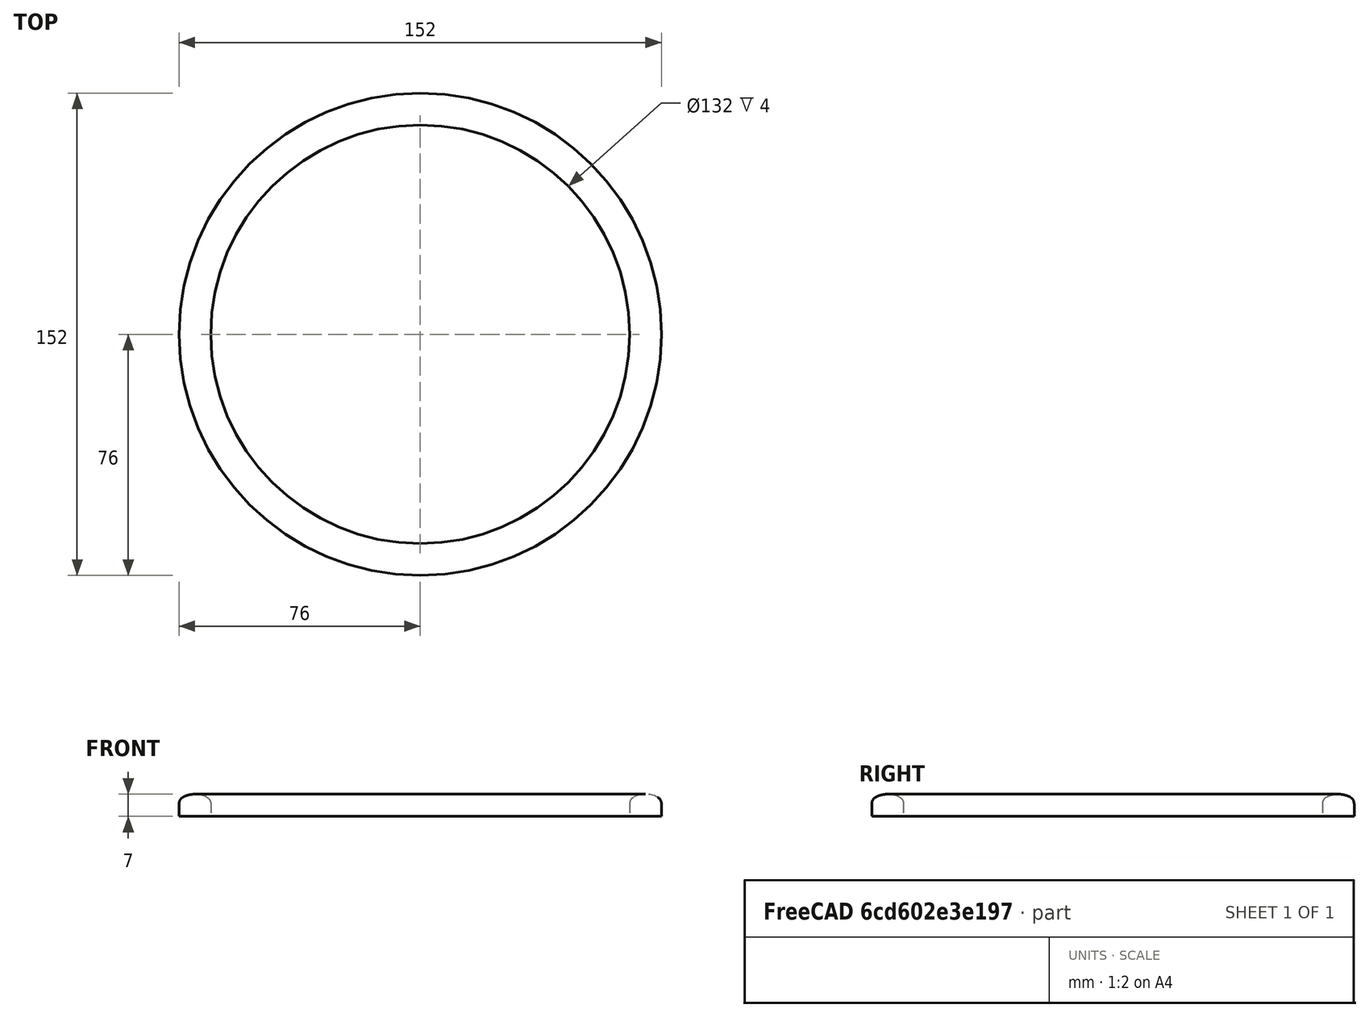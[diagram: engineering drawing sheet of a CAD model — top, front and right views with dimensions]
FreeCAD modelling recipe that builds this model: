
FCSTD DOCUMENT  (FreeCAD 0.18R14016 (Git))
Label: input_rim_test1
License: All rights reserved
LicenseURL: http://en.wikipedia.org/wiki/All_rights_reserved
objects: Sketcher::SketchObject×2, PartDesign::Revolution×1, PartDesign::Body×1, Part::Part2DObjectPython×1, TechDraw::DrawSVGTemplate×1, TechDraw::DrawViewPart×1, TechDraw::DrawPage×1
note: 6 computed .brp shape members not serialized (recipe doc carries the construction recipe); baked Part::Feature solids carry a one-line shape summary decoded from their .brp

FEATURE [Sketcher::SketchObject] Sketch  label="input_rim_base_Sketch"
  MapMode = 5
  Placement = pos=(0,0,0) rot=(1,0,0;1.5708rad)
  Support = -> [XZ_Plane]
  sketch-geometry (8):
    g0: LineSegment StartX=66 StartY=0 StartZ=0 EndX=76 EndY=0 EndZ=0
    g1: LineSegment [constr] StartX=66 StartY=0 StartZ=0 EndX=0 EndY=0 EndZ=0
    g2: LineSegment StartX=76 StartY=0 StartZ=0 EndX=76 EndY=4 EndZ=0
    g3: ArcOfCircle CenterX=73.6667 CenterY=4 CenterZ=0 NormalX=0 NormalY=0 NormalZ=1 AngleXU=0 Radius=2.33333 StartAngle=0 EndAngle=1.08084
    g4: ArcOfCircle CenterX=71 CenterY=-1 CenterZ=0 NormalX=0 NormalY=0 NormalZ=1 AngleXU=0 Radius=8 StartAngle=1.08084 EndAngle=2.06075
    g5: ArcOfCircle CenterX=68.3333 CenterY=4 CenterZ=0 NormalX=0 NormalY=0 NormalZ=1 AngleXU=0 Radius=2.33333 StartAngle=2.06075 EndAngle=3.14159
    g6: LineSegment StartX=66 StartY=4 StartZ=0 EndX=66 EndY=0 EndZ=0
    g7: LineSegment [constr] StartX=71 StartY=7 StartZ=0 EndX=71 EndY=0 EndZ=0
  constraints (22):
    c: Horizontal(g0)
    c: Coincident(g1,g0)
    c: Coincident(g1,g-1)
    c: Horizontal(g1)
    c: DistanceX(g0,g0) = 10
    c: Coincident(g0,g2)
    c: Vertical(g2)
    c: Tangent(g2,g3) = -1.5708
    c: Tangent(g3,g4) = -1.5708
    c: Tangent(g4,g5) = -1.5708
    c: Tangent(g5,g6) = -1.5708
    c: Coincident(g6,g0)
    c: Vertical(g6)
    c: Equal(g3,g5)
    c: Vertical(g7)
    c: Symmetric(g0,g0,g7)
    c: Perpendicular(g7,g4) = 4.71239
    c: DistanceY(g7,g7) = 7
    c: Radius(g5) = 2.33333
    c: DistanceX(g1,g1) = 66
    c: Radius(g4) = 8
    c: DistanceY(g2,g2) = 4
FEATURE [PartDesign::Revolution] Revolution
  Angle = 360
  Axis = (0,0,1)
  Base = (0,0,0)
  Placement = pos=(0,0,0) rot=(1,0,0;1.5708rad)
  Profile = -> Sketch
  ReferenceAxis = -> Z_Axis
FEATURE [Sketcher::SketchObject] Sketch001
  MapMode = 5
  Support = -> [XY_Plane]
FEATURE [PartDesign::Body] Body  label="input_rim_Body"
  Group = -> [Sketch,Revolution,Sketch001]
  Origin = -> Origin
  Tip = -> Revolution
FEATURE [Part::Part2DObjectPython] ShapeString  # Draft 2D object (typed FeaturePython)
  FontFile = <userpath>/mydata/vision/webfonts/fontsquirrel.com/almendra/Almendra-Regular.otf
  Placement = pos=(-66.2932,-19.1621,6.77092) rot=(0,0,1;0rad)
  Size = 8
  String = Hallo Welt :-)
  Tracking = 0
FEATURE [TechDraw::DrawSVGTemplate] Template001
  Height = 210
  Orientation = 1
  Width = 297
FEATURE [TechDraw::DrawViewPart] View
  CoarseView = false
  Direction = (0,0,1)
  Focus = 100
  HardHidden = false
  IsoCount = 0
  IsoHidden = false
  IsoVisible = false
  LockPosition = false
  Perspective = false
  Rotation = 0
  ScaleType = 0
  SeamHidden = false
  SeamVisible = false
  SmoothHidden = false
  SmoothVisible = false
  Source = -> [Body]
  X = 148.5
  Y = 105
FEATURE [TechDraw::DrawPage] Page001  label="CAM_Page"
  KeepUpdated = true
  ProjectionType = 0
  Template = -> Template001
  Views = -> [View]
